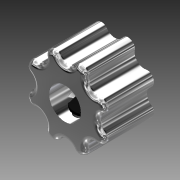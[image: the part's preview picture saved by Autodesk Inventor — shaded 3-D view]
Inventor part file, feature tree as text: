
AUTODESK INVENTOR PART (.ipt)
format: ipt  version: 2012 (Build 160160000, 160)  size: 1,621,504 bytes
history: native  units: in
note: dims shown in document units (in); Inventor stores cm internally (conversion verified against a paired STEP export)
features: hole x8, sketch x4, other x2, imported_body x2, fillet x2, move_body x1
ambient origin geometry x8: Origin, YZ Plane, XZ Plane, XY Plane, X Axis, Y Axis, Z Axis, Center Point
feature tree (19):
  parser-record x1  (decoder bookkeeping rows leaked as tree rows — omitted from the tree; the rows remain in map.json)
  imported_body  "Base1"
  imported_body  "Base2"
  sketch  "Sketch1"  dims[d0=0.125in d1=0.125in]
  sketch  "Sketch2"  dims[d2=0.125in d3=0.125in]
  sketch  "Sketch3"  dims[d4=45.0deg d5=0.0in]
  sketch  "Sketch4"  dims[d6=45.0deg d7=45.0deg d8=0.125in d9=0.125in d10=0.125in d11=0.125in d12=0.1in d13=0.75in d14=0.375in d15=0.25in d16=0.5635in d17=1.0in d18=0.8108in d19=0.1in d20=0.75in d21=0.375in d22=0.25in d23=0.5635in d24=1.0in d25=0.8108in d26=0.1in d27=0.75in d28=0.375in d29=0.25in d30=0.5635in d31=1.0in d32=0.8108in d33=0.1in d34=0.75in d35=0.375in d36=0.25in d37=0.5635in d38=1.0in d39=0.8108in d40=0.1in d41=0.75in d42=0.375in d43=0.25in d44=0.5635in d45=1.0in d46=0.8108in d47=0.1in d48=0.75in d49=0.375in d50=0.25in d51=0.5635in d52=1.0in d53=0.8108in d54=0.1in d55=0.75in d56=0.375in d57=0.25in d58=0.5635in d59=1.0in d60=0.8108in d61=0.1in d62=0.75in d63=0.375in d64=0.25in d65=0.5635in d66=1.0in d67=0.8108in d68=0.0in d69=0.04in d70=0.0in d71=0.03in d72=0.025in]
  hole  "Hole1"  [1 undecoded]
  hole  "Hole2"  [1 undecoded]
  hole  "Hole3"  [1 undecoded]
  hole  "Hole4"  [1 undecoded]
  hole  "Hole5"  [1 undecoded]
  hole  "Hole6"  [1 undecoded]
  hole  "Hole7"  [1 undecoded]
  hole  "Hole8"  [1 undecoded]
  move_body  "Move Body1"
  fillet  "Fillet1"  Radius=0.04in
  fillet  "Fillet2"  Radius=0.03in
  other  "NONE_1"
note: 8 required parameter values undecoded (feature->parameter linkage not recoverable at this tier; creation-order binding heuristic only, values carry confidence <= 0.55)
